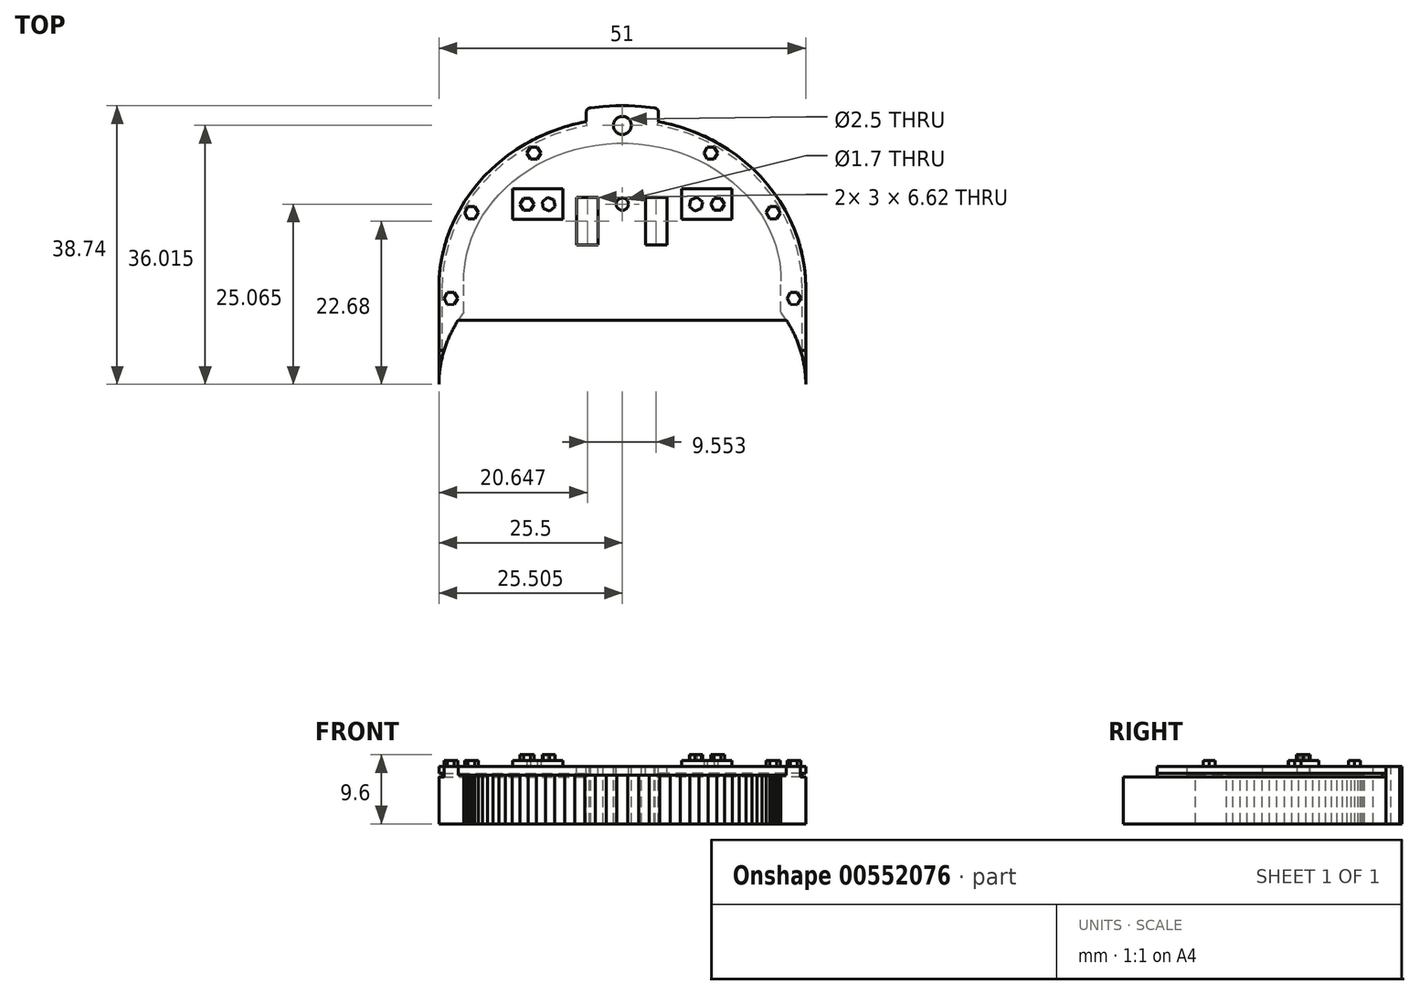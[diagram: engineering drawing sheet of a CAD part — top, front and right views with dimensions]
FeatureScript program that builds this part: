
annotation { "Feature Type Name" : "Feature", "Feature Type Description" : "" }
export const myFeature = defineFeature(function(context is Context, id is Id, definition is map)
    precondition{}
    {
        {
            var Q0;
            Q0=qCreatedBy(makeId("Top.planeOp"),FACE);
            var sketch = newSketch(context, id + "F0", { "sketchPlane" : qUnion([Q0])});
            skEllipticalArc(sketch, "E0", {});
            skEllipticalArc(sketch, "E1", {});
            skEllipticalArc(sketch, "E2", {});
            skLineSegment(sketch, "E3", {"start": v(-22.81, -10.43) * mm, "end": v(22.81, -10.43) * mm});
            skEllipticalArc(sketch, "E4", {});
            skLineSegment(sketch, "E5", {"start": v(5, 17.17) * mm, "end": v(5, 18.54) * mm});
            skArc(sketch, "E6", {"start": v(5, 18.54) * mm, "mid": v(4.88, 18.87) * mm, "end": v(4.58, 19.06) * mm});
            skLineSegment(sketch, "E7", {"start": v(4.58, 19.06) * mm, "end": v(4.43, 19.08) * mm});
            skArc(sketch, "E8", {"start": v(4.43, 19.08) * mm, "mid": v(4.42, 19.08) * mm, "end": v(4.4, 19.08) * mm});
            skLineSegment(sketch, "E9", {"start": v(4.4, 19.08) * mm, "end": v(2.66, 19.27) * mm});
            skLineSegment(sketch, "E10", {"start": v(2.66, 19.27) * mm, "end": v(0.89, 19.37) * mm});
            skLineSegment(sketch, "E11", {"start": v(0.89, 19.37) * mm, "end": v(-0.89, 19.37) * mm});
            skLineSegment(sketch, "E12", {"start": v(-0.89, 19.37) * mm, "end": v(-2.66, 19.27) * mm});
            skLineSegment(sketch, "E13", {"start": v(-2.66, 19.27) * mm, "end": v(-4.42, 19.08) * mm});
            skLineSegment(sketch, "E14", {"start": v(-4.42, 19.08) * mm, "end": v(-4.58, 19.06) * mm});
            skArc(sketch, "E15", {"start": v(-4.58, 19.06) * mm, "mid": v(-4.88, 18.87) * mm, "end": v(-5, 18.54) * mm});
            skLineSegment(sketch, "E16", {"start": v(-5, 18.54) * mm, "end": v(-5, 17.17) * mm});
            skLineSegment(sketch, "E17", {"start": v(-25.5, -5.65) * mm, "end": v(-25.5, -19.37) * mm});
            skLineSegment(sketch, "E18", {"start": v(25.5, -5.98) * mm, "end": v(25.5, -19.37) * mm});
            skCircle(sketch, "E19", {"center": v(0, 16.64) * mm, "radius": 1.25 * mm});
            skLineSegment(sketch, "E20", {"start": v(22.05, -5.06) * mm, "end": v(22.03, -4.07) * mm});
            skLineSegment(sketch, "E21", {"start": v(22.03, -4.07) * mm, "end": v(21.95, -3.1) * mm});
            skLineSegment(sketch, "E22", {"start": v(21.95, -3.1) * mm, "end": v(21.8, -2.1) * mm});
            skLineSegment(sketch, "E23", {"start": v(21.8, -2.1) * mm, "end": v(21.6, -1.1) * mm});
            skLineSegment(sketch, "E24", {"start": v(21.6, -1.1) * mm, "end": v(21.3, -0.06) * mm});
            skLineSegment(sketch, "E25", {"start": v(21.3, -0.06) * mm, "end": v(20.95, 0.98) * mm});
            skLineSegment(sketch, "E26", {"start": v(20.95, 0.98) * mm, "end": v(20.52, 2.02) * mm});
            skLineSegment(sketch, "E27", {"start": v(20.52, 2.02) * mm, "end": v(20, 3.05) * mm});
            skLineSegment(sketch, "E28", {"start": v(20, 3.05) * mm, "end": v(19.42, 4.07) * mm});
            skLineSegment(sketch, "E29", {"start": v(19.42, 4.07) * mm, "end": v(18.75, 5.07) * mm});
            skLineSegment(sketch, "E30", {"start": v(18.75, 5.07) * mm, "end": v(18, 6.05) * mm});
            skLineSegment(sketch, "E31", {"start": v(18, 6.05) * mm, "end": v(17.18, 7) * mm});
            skLineSegment(sketch, "E32", {"start": v(17.18, 7) * mm, "end": v(16.27, 7.92) * mm});
            skLineSegment(sketch, "E33", {"start": v(16.27, 7.92) * mm, "end": v(15.3, 8.8) * mm});
            skLineSegment(sketch, "E34", {"start": v(15.3, 8.8) * mm, "end": v(14.24, 9.62) * mm});
            skLineSegment(sketch, "E35", {"start": v(14.24, 9.62) * mm, "end": v(13.12, 10.4) * mm});
            skLineSegment(sketch, "E36", {"start": v(13.12, 10.4) * mm, "end": v(11.93, 11.11) * mm});
            skLineSegment(sketch, "E37", {"start": v(11.93, 11.11) * mm, "end": v(10.68, 11.76) * mm});
            skLineSegment(sketch, "E38", {"start": v(10.68, 11.76) * mm, "end": v(9.38, 12.35) * mm});
            skLineSegment(sketch, "E39", {"start": v(9.38, 12.35) * mm, "end": v(8.03, 12.85) * mm});
            skLineSegment(sketch, "E40", {"start": v(8.03, 12.85) * mm, "end": v(6.64, 13.29) * mm});
            skLineSegment(sketch, "E41", {"start": v(6.64, 13.29) * mm, "end": v(5.2, 13.64) * mm});
            skLineSegment(sketch, "E42", {"start": v(5.2, 13.64) * mm, "end": v(3.74, 13.9) * mm});
            skLineSegment(sketch, "E43", {"start": v(3.74, 13.9) * mm, "end": v(2.26, 14.08) * mm});
            skLineSegment(sketch, "E44", {"start": v(2.26, 14.08) * mm, "end": v(0.75, 14.17) * mm});
            skLineSegment(sketch, "E45", {"start": v(0.75, 14.17) * mm, "end": v(-0.75, 14.17) * mm});
            skLineSegment(sketch, "E46", {"start": v(-0.75, 14.17) * mm, "end": v(-2.26, 14.08) * mm});
            skLineSegment(sketch, "E47", {"start": v(-2.26, 14.08) * mm, "end": v(-3.74, 13.9) * mm});
            skLineSegment(sketch, "E48", {"start": v(-3.74, 13.9) * mm, "end": v(-5.2, 13.64) * mm});
            skLineSegment(sketch, "E49", {"start": v(-5.2, 13.64) * mm, "end": v(-6.64, 13.29) * mm});
            skLineSegment(sketch, "E50", {"start": v(-6.64, 13.29) * mm, "end": v(-8.03, 12.85) * mm});
            skLineSegment(sketch, "E51", {"start": v(-8.03, 12.85) * mm, "end": v(-9.38, 12.35) * mm});
            skLineSegment(sketch, "E52", {"start": v(-9.38, 12.35) * mm, "end": v(-10.68, 11.76) * mm});
            skLineSegment(sketch, "E53", {"start": v(-10.68, 11.76) * mm, "end": v(-11.93, 11.11) * mm});
            skLineSegment(sketch, "E54", {"start": v(-11.93, 11.11) * mm, "end": v(-13.12, 10.4) * mm});
            skLineSegment(sketch, "E55", {"start": v(-13.12, 10.4) * mm, "end": v(-14.24, 9.62) * mm});
            skLineSegment(sketch, "E56", {"start": v(-14.24, 9.62) * mm, "end": v(-15.3, 8.8) * mm});
            skLineSegment(sketch, "E57", {"start": v(-15.3, 8.8) * mm, "end": v(-16.27, 7.92) * mm});
            skLineSegment(sketch, "E58", {"start": v(-16.27, 7.92) * mm, "end": v(-17.18, 7) * mm});
            skLineSegment(sketch, "E59", {"start": v(-17.18, 7) * mm, "end": v(-18, 6.05) * mm});
            skLineSegment(sketch, "E60", {"start": v(-18, 6.05) * mm, "end": v(-18.75, 5.07) * mm});
            skLineSegment(sketch, "E61", {"start": v(-18.75, 5.07) * mm, "end": v(-19.42, 4.07) * mm});
            skLineSegment(sketch, "E62", {"start": v(-19.42, 4.07) * mm, "end": v(-20, 3.05) * mm});
            skLineSegment(sketch, "E63", {"start": v(-20, 3.05) * mm, "end": v(-20.52, 2.02) * mm});
            skLineSegment(sketch, "E64", {"start": v(-20.52, 2.02) * mm, "end": v(-20.95, 0.98) * mm});
            skLineSegment(sketch, "E65", {"start": v(-20.95, 0.98) * mm, "end": v(-21.3, -0.06) * mm});
            skLineSegment(sketch, "E66", {"start": v(-21.3, -0.06) * mm, "end": v(-21.6, -1.1) * mm});
            skLineSegment(sketch, "E67", {"start": v(-21.6, -1.1) * mm, "end": v(-21.8, -2.1) * mm});
            skLineSegment(sketch, "E68", {"start": v(-21.8, -2.1) * mm, "end": v(-21.95, -3.1) * mm});
            skLineSegment(sketch, "E69", {"start": v(-21.95, -3.1) * mm, "end": v(-22.03, -4.07) * mm});
            skLineSegment(sketch, "E70", {"start": v(-22.03, -4.07) * mm, "end": v(-22.05, -5.06) * mm});
            skLineSegment(sketch, "E71", {"start": v(-22.05, -4.56) * mm, "end": v(-22.05, -10.43) * mm});
            skLineSegment(sketch, "E72", {"start": v(22.05, -5) * mm, "end": v(22.05, -10.43) * mm});
            skLineSegment(sketch, "E73", {"start": v(15.25, 3.57) * mm, "end": v(15.25, 7.82) * mm});
            skLineSegment(sketch, "E74", {"start": v(-15.25, 3.57) * mm, "end": v(-15.25, 7.82) * mm});
            skLineSegment(sketch, "E75", {"start": v(-8.25, 3.57) * mm, "end": v(-8.25, 7.82) * mm});
            skLineSegment(sketch, "E76", {"start": v(8.25, 3.57) * mm, "end": v(8.25, 7.82) * mm});
            skCircle(sketch, "E77", {"center": v(0, 5.7) * mm, "radius": 0.85 * mm});
            skLineSegment(sketch, "E78", {"start": v(-12.3, 5.7) * mm, "end": v(-12.77, 6.53) * mm});
            skLineSegment(sketch, "E79", {"start": v(-12.77, 6.53) * mm, "end": v(-13.73, 6.52) * mm});
            skLineSegment(sketch, "E80", {"start": v(-13.73, 6.52) * mm, "end": v(-14.2, 5.7) * mm});
            skLineSegment(sketch, "E81", {"start": v(-14.2, 5.7) * mm, "end": v(-13.73, 4.86) * mm});
            skLineSegment(sketch, "E82", {"start": v(-13.73, 4.86) * mm, "end": v(-12.77, 4.86) * mm});
            skLineSegment(sketch, "E83", {"start": v(-12.77, 4.86) * mm, "end": v(-12.3, 5.7) * mm});
            skLineSegment(sketch, "E84", {"start": v(-10.99, 5.08) * mm, "end": v(-11.15, 6.03) * mm});
            skLineSegment(sketch, "E85", {"start": v(-11.15, 6.03) * mm, "end": v(-10.41, 6.64) * mm});
            skLineSegment(sketch, "E86", {"start": v(-10.41, 6.64) * mm, "end": v(-9.51, 6.3) * mm});
            skLineSegment(sketch, "E87", {"start": v(-9.51, 6.3) * mm, "end": v(-9.35, 5.36) * mm});
            skLineSegment(sketch, "E88", {"start": v(-9.35, 5.36) * mm, "end": v(-10.09, 4.75) * mm});
            skLineSegment(sketch, "E89", {"start": v(-10.09, 4.75) * mm, "end": v(-10.99, 5.08) * mm});
            skLineSegment(sketch, "E90", {"start": v(12.3, 5.7) * mm, "end": v(12.77, 6.53) * mm});
            skLineSegment(sketch, "E91", {"start": v(12.77, 6.53) * mm, "end": v(13.73, 6.52) * mm});
            skLineSegment(sketch, "E92", {"start": v(13.73, 6.52) * mm, "end": v(14.2, 5.7) * mm});
            skLineSegment(sketch, "E93", {"start": v(14.2, 5.7) * mm, "end": v(13.73, 4.86) * mm});
            skLineSegment(sketch, "E94", {"start": v(13.73, 4.86) * mm, "end": v(12.77, 4.86) * mm});
            skLineSegment(sketch, "E95", {"start": v(12.77, 4.86) * mm, "end": v(12.3, 5.7) * mm});
            skLineSegment(sketch, "E96", {"start": v(10.99, 5.08) * mm, "end": v(11.15, 6.03) * mm});
            skLineSegment(sketch, "E97", {"start": v(11.15, 6.03) * mm, "end": v(10.41, 6.64) * mm});
            skLineSegment(sketch, "E98", {"start": v(10.41, 6.64) * mm, "end": v(9.51, 6.3) * mm});
            skLineSegment(sketch, "E99", {"start": v(9.51, 6.3) * mm, "end": v(9.35, 5.36) * mm});
            skLineSegment(sketch, "E100", {"start": v(9.35, 5.36) * mm, "end": v(10.09, 4.75) * mm});
            skLineSegment(sketch, "E101", {"start": v(10.09, 4.75) * mm, "end": v(10.99, 5.08) * mm});
            skLineSegment(sketch, "E102", {"start": v(-22.89, -7.42) * mm, "end": v(-23.37, -6.6) * mm});
            skLineSegment(sketch, "E103", {"start": v(-23.37, -6.6) * mm, "end": v(-24.33, -6.6) * mm});
            skLineSegment(sketch, "E104", {"start": v(-24.33, -6.6) * mm, "end": v(-24.8, -7.43) * mm});
            skLineSegment(sketch, "E105", {"start": v(-24.8, -7.43) * mm, "end": v(-24.32, -8.26) * mm});
            skLineSegment(sketch, "E106", {"start": v(-24.32, -8.26) * mm, "end": v(-23.36, -8.26) * mm});
            skLineSegment(sketch, "E107", {"start": v(-23.36, -8.26) * mm, "end": v(-22.89, -7.42) * mm});
            skLineSegment(sketch, "E108", {"start": v(-20.02, 4.5) * mm, "end": v(-20.5, 5.34) * mm});
            skLineSegment(sketch, "E109", {"start": v(-20.5, 5.34) * mm, "end": v(-21.46, 5.33) * mm});
            skLineSegment(sketch, "E110", {"start": v(-21.46, 5.33) * mm, "end": v(-21.94, 4.5) * mm});
            skLineSegment(sketch, "E111", {"start": v(-21.94, 4.5) * mm, "end": v(-21.46, 3.67) * mm});
            skLineSegment(sketch, "E112", {"start": v(-21.46, 3.67) * mm, "end": v(-20.5, 3.67) * mm});
            skLineSegment(sketch, "E113", {"start": v(-20.5, 3.67) * mm, "end": v(-20.02, 4.5) * mm});
            skLineSegment(sketch, "E114", {"start": v(-11.34, 12.77) * mm, "end": v(-11.82, 13.6) * mm});
            skLineSegment(sketch, "E115", {"start": v(-11.82, 13.6) * mm, "end": v(-12.78, 13.6) * mm});
            skLineSegment(sketch, "E116", {"start": v(-12.78, 13.6) * mm, "end": v(-13.26, 12.77) * mm});
            skLineSegment(sketch, "E117", {"start": v(-13.26, 12.77) * mm, "end": v(-12.78, 11.94) * mm});
            skLineSegment(sketch, "E118", {"start": v(-12.78, 11.94) * mm, "end": v(-11.82, 11.94) * mm});
            skLineSegment(sketch, "E119", {"start": v(-11.82, 11.94) * mm, "end": v(-11.34, 12.77) * mm});
            skLineSegment(sketch, "E120", {"start": v(22.89, -7.42) * mm, "end": v(23.37, -6.6) * mm});
            skLineSegment(sketch, "E121", {"start": v(23.37, -6.6) * mm, "end": v(24.33, -6.6) * mm});
            skLineSegment(sketch, "E122", {"start": v(24.33, -6.6) * mm, "end": v(24.8, -7.43) * mm});
            skLineSegment(sketch, "E123", {"start": v(24.8, -7.43) * mm, "end": v(24.32, -8.26) * mm});
            skLineSegment(sketch, "E124", {"start": v(24.32, -8.26) * mm, "end": v(23.36, -8.26) * mm});
            skLineSegment(sketch, "E125", {"start": v(23.36, -8.26) * mm, "end": v(22.89, -7.42) * mm});
            skLineSegment(sketch, "E126", {"start": v(-15.25, 7.82) * mm, "end": v(-8.25, 7.82) * mm});
            skLineSegment(sketch, "E127", {"start": v(8.25, 7.82) * mm, "end": v(15.25, 7.82) * mm});
            skLineSegment(sketch, "E128", {"start": v(-15.25, 3.57) * mm, "end": v(-8.25, 3.57) * mm});
            skLineSegment(sketch, "E129", {"start": v(8.25, 3.57) * mm, "end": v(15.25, 3.57) * mm});
            skLineSegment(sketch, "E130", {"start": v(3.2, 2.22) * mm, "end": v(3.2, 14) * mm});
            skLineSegment(sketch, "E131", {"start": v(-3.35, 2.22) * mm, "end": v(-3.35, 14) * mm});
            skLineSegment(sketch, "E132", {"start": v(20.02, 4.5) * mm, "end": v(20.5, 5.34) * mm});
            skLineSegment(sketch, "E133", {"start": v(20.5, 5.34) * mm, "end": v(21.46, 5.33) * mm});
            skLineSegment(sketch, "E134", {"start": v(21.46, 5.33) * mm, "end": v(21.94, 4.5) * mm});
            skLineSegment(sketch, "E135", {"start": v(21.94, 4.5) * mm, "end": v(21.46, 3.67) * mm});
            skLineSegment(sketch, "E136", {"start": v(21.46, 3.67) * mm, "end": v(20.5, 3.67) * mm});
            skLineSegment(sketch, "E137", {"start": v(20.5, 3.67) * mm, "end": v(20.02, 4.5) * mm});
            skLineSegment(sketch, "E138", {"start": v(11.34, 12.77) * mm, "end": v(11.82, 13.6) * mm});
            skLineSegment(sketch, "E139", {"start": v(11.82, 13.6) * mm, "end": v(12.78, 13.6) * mm});
            skLineSegment(sketch, "E140", {"start": v(12.78, 13.6) * mm, "end": v(13.26, 12.77) * mm});
            skLineSegment(sketch, "E141", {"start": v(13.26, 12.77) * mm, "end": v(12.78, 11.94) * mm});
            skLineSegment(sketch, "E142", {"start": v(12.78, 11.94) * mm, "end": v(11.82, 11.94) * mm});
            skLineSegment(sketch, "E143", {"start": v(11.82, 11.94) * mm, "end": v(11.34, 12.77) * mm});
            skFitSpline(sketch, "E144.0", {"points": [v(25, -5.98) * mm, v(25, -4.46) * mm, v(24.76, -2.2) * mm, v(23.97, 0.72) * mm, v(23.14, 2.86) * mm, v(22.1, 4.91) * mm, v(20.4, 7.52) * mm, v(17.8, 10.45) * mm, v(14.64, 12.86) * mm, v(11.81, 14.43) * mm, v(8.85, 15.73) * mm, v(5.7, 16.6) * mm, v(2.47, 17.06) * mm, v(0, 17.17) * mm, v(-2.47, 17.06) * mm, v(-5.7, 16.6) * mm, v(-8.85, 15.73) * mm, v(-11.81, 14.43) * mm, v(-14.64, 12.86) * mm, v(-17.8, 10.45) * mm, v(-20.4, 7.52) * mm, v(-22.1, 4.91) * mm, v(-23.14, 2.86) * mm, v(-23.97, 0.72) * mm, v(-24.76, -2.2) * mm, v(-25, -4.46) * mm, v(-25, -5.98) * mm]});
            skLineSegment(sketch, "E145", {"start": v(-8.4, 6.62) * mm, "end": v(8.1, 6.62) * mm, "construction": true});
            skLineSegment(sketch, "E146.bottom", {"start": v(-3.35, 6.62) * mm, "end": v(-6.35, 6.62) * mm});
            skLineSegment(sketch, "E146.top", {"start": v(-3.35, 0) * mm, "end": v(-6.35, 0) * mm});
            skLineSegment(sketch, "E146.left", {"start": v(-3.35, 6.62) * mm, "end": v(-3.35, 0) * mm});
            skLineSegment(sketch, "E146.right", {"start": v(-6.35, 6.62) * mm, "end": v(-6.35, 0) * mm});
            skLineSegment(sketch, "E147.bottom", {"start": v(3.2, 6.62) * mm, "end": v(6.2, 6.62) * mm});
            skLineSegment(sketch, "E147.top", {"start": v(3.2, 0) * mm, "end": v(6.2, 0) * mm});
            skLineSegment(sketch, "E147.left", {"start": v(3.2, 6.62) * mm, "end": v(3.2, 0) * mm});
            skLineSegment(sketch, "E147.right", {"start": v(6.2, 6.62) * mm, "end": v(6.2, 0) * mm});
            const initialGuessF0  = {"E0": [0, -0.019369520999999994, 25.5, 0, 0.0255, 0.02, 2.615361, 3.141593], "E1": [0, -0.017619520999999992, 25.5, 0, 0.0255, 0.02, 1.444974, 1.696618], "E2": [0, -0.019369520999999994, 25.5, 0, 0.0255, 0.02, 0, 0.526232], "E4": [0, -0.005982601999999986, 25.5, 0, 0.0255, 0.023613081, 0, 3.141593]};
            skSetInitialGuess(sketch, initialGuessF0);
            skSolve(sketch);
        }
        {
            var Q0;
            {var subQ19=sQuery(id+"F0.wireOp",EDGE,"E18");Q0=makeQuery(id+"F0.imprint","IMPRINT",FACE,{"disambiguationData":[TD([[makeQuery(id+"F0.imprint","IMPRINT",EDGE,{"derivedFrom":subQ19}),-1.0]])]});}
            var Q1;
            Q1=makeQuery(id+"F0.imprint","IMPRINT",FACE,{"disambiguationData":[TD([[makeQuery(id+"F0.imprint","IMPRINT",EDGE,{"derivedFrom":sQuery(id+"F0.wireOp",EDGE,"E102")}),1.0]])]});
            var Q2;
            Q2=makeQuery(id+"F0.imprint","IMPRINT",FACE,{"disambiguationData":[TD([[makeQuery(id+"F0.imprint","IMPRINT",EDGE,{"derivedFrom":sQuery(id+"F0.wireOp",EDGE,"E108")}),1.0]])]});
            var Q3;
            Q3=makeQuery(id+"F0.imprint","IMPRINT",FACE,{"disambiguationData":[TD([[makeQuery(id+"F0.imprint","IMPRINT",EDGE,{"derivedFrom":sQuery(id+"F0.wireOp",EDGE,"E114")}),1.0]])]});
            var Q4;
            Q4=makeQuery(id+"F0.imprint","IMPRINT",FACE,{"disambiguationData":[TD([[makeQuery(id+"F0.imprint","IMPRINT",EDGE,{"derivedFrom":sQuery(id+"F0.wireOp",EDGE,"E138")}),-1.0]])]});
            var Q5;
            Q5=makeQuery(id+"F0.imprint","IMPRINT",FACE,{"disambiguationData":[TD([[makeQuery(id+"F0.imprint","IMPRINT",EDGE,{"derivedFrom":sQuery(id+"F0.wireOp",EDGE,"E132")}),-1.0]])]});
            var Q6;
            Q6=makeQuery(id+"F0.imprint","IMPRINT",FACE,{"disambiguationData":[TD([[makeQuery(id+"F0.imprint","IMPRINT",EDGE,{"derivedFrom":sQuery(id+"F0.wireOp",EDGE,"E120")}),-1.0]])]});
            var Q7;
            {var subQ1=sQuery(id+"F0.wireOp",EDGE,"E1");Q7=makeQuery(id+"F0.imprint","IMPRINT",FACE,{"disambiguationData":[TD([[makeQuery(id+"F0.imprint","IMPRINT",EDGE,{"derivedFrom":subQ1}),-1.0]])]});}
            var Q8;
            {var subQ0=sQuery(id+"F0.wireOp",EDGE,"E5");Q8=makeQuery(id+"F0.imprint","IMPRINT",FACE,{"disambiguationData":[TD([[makeQuery(id+"F0.imprint","IMPRINT",EDGE,{"derivedFrom":subQ0}),1.0]])]});}
            extrude(context, id + "F1", {"entities" : qUnion([Q0, Q1, Q2, Q3, Q4, Q5, Q6, Q7, Q8]), "oppositeDirection" : true, "depth" : 8 * mm, "offsetDistance" : 25.4 * mm});
        }
        {
            var Q0;
            Q0 = qSketchRegion(id + "F0", true);
            var Q1;
            Q1=makeQuery(id+"F0.imprint","IMPRINT",FACE,{"disambiguationData":[TD([[makeQuery(id+"F0.imprint","IMPRINT",EDGE,{"derivedFrom":sQuery(id+"F0.wireOp",EDGE,"E74")}),-1.0]])]});
            var Q2;
            Q2=makeQuery(id+"F0.imprint","IMPRINT",FACE,{"disambiguationData":[TD([[makeQuery(id+"F0.imprint","IMPRINT",EDGE,{"derivedFrom":sQuery(id+"F0.wireOp",EDGE,"E78")}),1.0]])]});
            var Q3;
            Q3=makeQuery(id+"F0.imprint","IMPRINT",FACE,{"disambiguationData":[TD([[makeQuery(id+"F0.imprint","IMPRINT",EDGE,{"derivedFrom":sQuery(id+"F0.wireOp",EDGE,"E84")}),-1.0]])]});
            var Q4;
            Q4=makeQuery(id+"F0.imprint","IMPRINT",FACE,{"disambiguationData":[TD([[makeQuery(id+"F0.imprint","IMPRINT",EDGE,{"derivedFrom":sQuery(id+"F0.wireOp",EDGE,"E73")}),1.0]])]});
            var Q5;
            Q5=makeQuery(id+"F0.imprint","IMPRINT",FACE,{"disambiguationData":[TD([[makeQuery(id+"F0.imprint","IMPRINT",EDGE,{"derivedFrom":sQuery(id+"F0.wireOp",EDGE,"E96")}),1.0]])]});
            var Q6;
            Q6=makeQuery(id+"F0.imprint","IMPRINT",FACE,{"disambiguationData":[TD([[makeQuery(id+"F0.imprint","IMPRINT",EDGE,{"derivedFrom":sQuery(id+"F0.wireOp",EDGE,"E90")}),-1.0]])]});
            extrude(context, id + "F2", {"entities" : qUnion([Q0, Q1, Q2, Q3, Q4, Q5, Q6]), "operationType" : NewBodyOperationType.ADD, "oppositeDirection" : true, "depth" : 1.2 * mm, "offsetDistance" : 25 * mm});
        }
        {
            var Q0;
            Q0=makeQuery(id+"F0.imprint","IMPRINT",FACE,{"disambiguationData":[TD([[makeQuery(id+"F0.imprint","IMPRINT",EDGE,{"derivedFrom":sQuery(id+"F0.wireOp",EDGE,"E73")}),1.0]])]});
            var Q1;
            Q1=makeQuery(id+"F0.imprint","IMPRINT",FACE,{"disambiguationData":[TD([[makeQuery(id+"F0.imprint","IMPRINT",EDGE,{"derivedFrom":sQuery(id+"F0.wireOp",EDGE,"E74")}),-1.0]])]});
            extrude(context, id + "F3", {"entities" : qUnion([Q0, Q1]), "operationType" : NewBodyOperationType.ADD, "depth" : .8 * mm, "offsetDistance" : 25 * mm});
        }
        {
            var Q0;
            Q0=makeQuery(id+"F0.imprint","IMPRINT",FACE,{"disambiguationData":[TD([[makeQuery(id+"F0.imprint","IMPRINT",EDGE,{"derivedFrom":sQuery(id+"F0.wireOp",EDGE,"E78")}),1.0]])]});
            var Q1;
            Q1=makeQuery(id+"F0.imprint","IMPRINT",FACE,{"disambiguationData":[TD([[makeQuery(id+"F0.imprint","IMPRINT",EDGE,{"derivedFrom":sQuery(id+"F0.wireOp",EDGE,"E84")}),-1.0]])]});
            var Q2;
            Q2=makeQuery(id+"F0.imprint","IMPRINT",FACE,{"disambiguationData":[TD([[makeQuery(id+"F0.imprint","IMPRINT",EDGE,{"derivedFrom":sQuery(id+"F0.wireOp",EDGE,"E96")}),1.0]])]});
            var Q3;
            Q3=makeQuery(id+"F0.imprint","IMPRINT",FACE,{"disambiguationData":[TD([[makeQuery(id+"F0.imprint","IMPRINT",EDGE,{"derivedFrom":sQuery(id+"F0.wireOp",EDGE,"E90")}),-1.0]])]});
            extrude(context, id + "F4", {"entities" : qUnion([Q0, Q1, Q2, Q3]), "operationType" : NewBodyOperationType.ADD, "depth" : 1.6 * mm, "offsetDistance" : 25 * mm});
        }
        {
            var Q0;
            Q0=makeQuery(id+"F0.imprint","IMPRINT",FACE,{"disambiguationData":[TD([[makeQuery(id+"F0.imprint","IMPRINT",EDGE,{"derivedFrom":sQuery(id+"F0.wireOp",EDGE,"E102")}),1.0]])]});
            var Q1;
            Q1=makeQuery(id+"F0.imprint","IMPRINT",FACE,{"disambiguationData":[TD([[makeQuery(id+"F0.imprint","IMPRINT",EDGE,{"derivedFrom":sQuery(id+"F0.wireOp",EDGE,"E108")}),1.0]])]});
            var Q2;
            Q2=makeQuery(id+"F0.imprint","IMPRINT",FACE,{"disambiguationData":[TD([[makeQuery(id+"F0.imprint","IMPRINT",EDGE,{"derivedFrom":sQuery(id+"F0.wireOp",EDGE,"E114")}),1.0]])]});
            var Q3;
            Q3=makeQuery(id+"F0.imprint","IMPRINT",FACE,{"disambiguationData":[TD([[makeQuery(id+"F0.imprint","IMPRINT",EDGE,{"derivedFrom":sQuery(id+"F0.wireOp",EDGE,"E138")}),-1.0]])]});
            var Q4;
            Q4=makeQuery(id+"F0.imprint","IMPRINT",FACE,{"disambiguationData":[TD([[makeQuery(id+"F0.imprint","IMPRINT",EDGE,{"derivedFrom":sQuery(id+"F0.wireOp",EDGE,"E132")}),-1.0]])]});
            var Q5;
            Q5=makeQuery(id+"F0.imprint","IMPRINT",FACE,{"disambiguationData":[TD([[makeQuery(id+"F0.imprint","IMPRINT",EDGE,{"derivedFrom":sQuery(id+"F0.wireOp",EDGE,"E120")}),-1.0]])]});
            extrude(context, id + "F5", {"entities" : qUnion([Q0, Q1, Q2, Q3, Q4, Q5]), "operationType" : NewBodyOperationType.ADD, "depth" : .8 * mm, "offsetDistance" : 25 * mm});
        }
        {
            var Q0;
            Q0=makeQuery(id+"F1.opExtrude","SWEPT_FACE",FACE,{"disambiguationData":[OSD([sQuery(id+"F0.wireOp",EDGE,"E18")])]});
            var sketch = newSketch(context, id + "F6", { "sketchPlane" : qUnion([Q0])});
            skLineSegment(sketch, "E148.bottom", {"start": v(-19.37, 0) * mm, "end": v(-14.62, 0) * mm});
            skLineSegment(sketch, "E148.top", {"start": v(-19.37, -1.5) * mm, "end": v(-14.62, -1.5) * mm});
            skLineSegment(sketch, "E148.left", {"start": v(-19.37, 0) * mm, "end": v(-19.37, -1.5) * mm});
            skLineSegment(sketch, "E148.right", {"start": v(-14.62, 0) * mm, "end": v(-14.62, -1.5) * mm});
            skSolve(sketch);
        }
        {
            var Q0;
            Q0=makeQuery(id+"F6.imprint","IMPRINT",FACE,{"disambiguationData":[TD([[makeQuery(id+"F6.imprint","IMPRINT",EDGE,{"derivedFrom":sQuery(id+"F6.wireOp",EDGE,"E148.bottom")}),1.0]])]});
            extrude(context, id + "F7", {"entities" : qUnion([Q0]), "operationType" : NewBodyOperationType.REMOVE, "oppositeDirection" : true, "depth" : 56 * mm, "offsetDistance" : 25 * mm});
        }
        {
            var Q0;
            Q0=makeQuery(id+"F1.opExtrude","SWEPT_FACE",FACE,{"disambiguationData":[OSD([sQuery(id+"F0.wireOp",EDGE,"E18")])]});
            var sketch = newSketch(context, id + "F8", { "sketchPlane" : qUnion([Q0])});
            skLineSegment(sketch, "E149.bottom", {"start": v(-14.62, -1.5) * mm, "end": v(-5.98, -1.5) * mm});
            skLineSegment(sketch, "E149.top", {"start": v(-14.62, -1) * mm, "end": v(-5.98, -1) * mm});
            skLineSegment(sketch, "E149.left", {"start": v(-14.62, -1.5) * mm, "end": v(-14.62, -1) * mm});
            skLineSegment(sketch, "E149.right", {"start": v(-5.98, -1.5) * mm, "end": v(-5.98, -1) * mm});
            skSolve(sketch);
        }
        {
            var Q0;
            Q0=makeQuery(id+"F8.imprint","IMPRINT",FACE,{"disambiguationData":[TD([[makeQuery(id+"F8.imprint","IMPRINT",EDGE,{"derivedFrom":sQuery(id+"F8.wireOp",EDGE,"E149.bottom")}),1.0]])]});
            extrude(context, id + "F9", {"entities" : qUnion([Q0]), "operationType" : NewBodyOperationType.REMOVE, "oppositeDirection" : true, "depth" : .5 * mm, "offsetDistance" : 25 * mm});
        }
        {
            var Q0;
            Q0=makeQuery(id+"F9.boolean.opBoolean","COPY",FACE,{"derivedFrom":makeQuery(id+"F9.opExtrude","SWEPT_FACE",FACE,{"disambiguationData":[OSD([sQuery(id+"F8.wireOp",EDGE,"E149.right")])]})});
            var Q1;
            {var subQ0=sQuery(id+"F0.wireOp",EDGE,"E4");Q1=makeQuery(id+"F1.opExtrude","CAP_EDGE",EDGE,{"disambiguationData":[OSD([subQ0]),TDD([makeQuery(id+"F0.imprint","IMPRINT",EDGE,{"disambiguationData":[TD([[makeQuery(id+"F0.imprint","INTERSECT",VERTEX,{"derivedFrom":[subQ0,sQuery(id+"F0.wireOp",EDGE,"E18")]}),-1.0]])],"derivedFrom":subQ0})])],"isStart":true});}
            sweep(context, id + "F10", {"operationType" : NewBodyOperationType.REMOVE, "profiles" : qUnion([Q0]), "path" : qUnion([Q1])});
        }
        {
            var Q0;
            Q0=makeQuery(id+"F1.opExtrude","SWEPT_FACE",FACE,{"disambiguationData":[OSD([sQuery(id+"F0.wireOp",EDGE,"E17")])]});
            var sketch = newSketch(context, id + "F11", { "sketchPlane" : qUnion([Q0])});
            skLineSegment(sketch, "E150.bottom", {"start": v(14.62, -1.5) * mm, "end": v(5.98, -1.5) * mm});
            skLineSegment(sketch, "E150.top", {"start": v(14.62, -1) * mm, "end": v(5.98, -1) * mm});
            skLineSegment(sketch, "E150.left", {"start": v(14.62, -1.5) * mm, "end": v(14.62, -1) * mm});
            skLineSegment(sketch, "E150.right", {"start": v(5.98, -1.5) * mm, "end": v(5.98, -1) * mm});
            skSolve(sketch);
        }
        {
            var Q0;
            Q0=makeQuery(id+"F11.imprint","IMPRINT",FACE,{"disambiguationData":[TD([[makeQuery(id+"F11.imprint","IMPRINT",EDGE,{"derivedFrom":sQuery(id+"F11.wireOp",EDGE,"E150.bottom")}),-1.0]])]});
            extrude(context, id + "F12", {"entities" : qUnion([Q0]), "operationType" : NewBodyOperationType.REMOVE, "oppositeDirection" : true, "depth" : .5 * mm, "offsetDistance" : 25 * mm});
        }
        {
            var Q0;
            Q0=makeQuery(id+"F12.boolean.opBoolean","COPY",FACE,{"derivedFrom":makeQuery(id+"F12.opExtrude","SWEPT_FACE",FACE,{"disambiguationData":[OSD([sQuery(id+"F11.wireOp",EDGE,"E150.right")])]})});
            var Q1;
            {var subQ0=sQuery(id+"F0.wireOp",EDGE,"E4");Q1=makeQuery(id+"F1.opExtrude","CAP_EDGE",EDGE,{"disambiguationData":[OSD([subQ0]),TDD([makeQuery(id+"F0.imprint","IMPRINT",EDGE,{"disambiguationData":[TD([[makeQuery(id+"F0.imprint","INTERSECT",VERTEX,{"derivedFrom":[subQ0,sQuery(id+"F0.wireOp",EDGE,"E17")]}),1.0]])],"derivedFrom":subQ0})])],"isStart":true});}
            sweep(context, id + "F13", {"operationType" : NewBodyOperationType.REMOVE, "profiles" : qUnion([Q0]), "path" : qUnion([Q1])});
        }
    });
